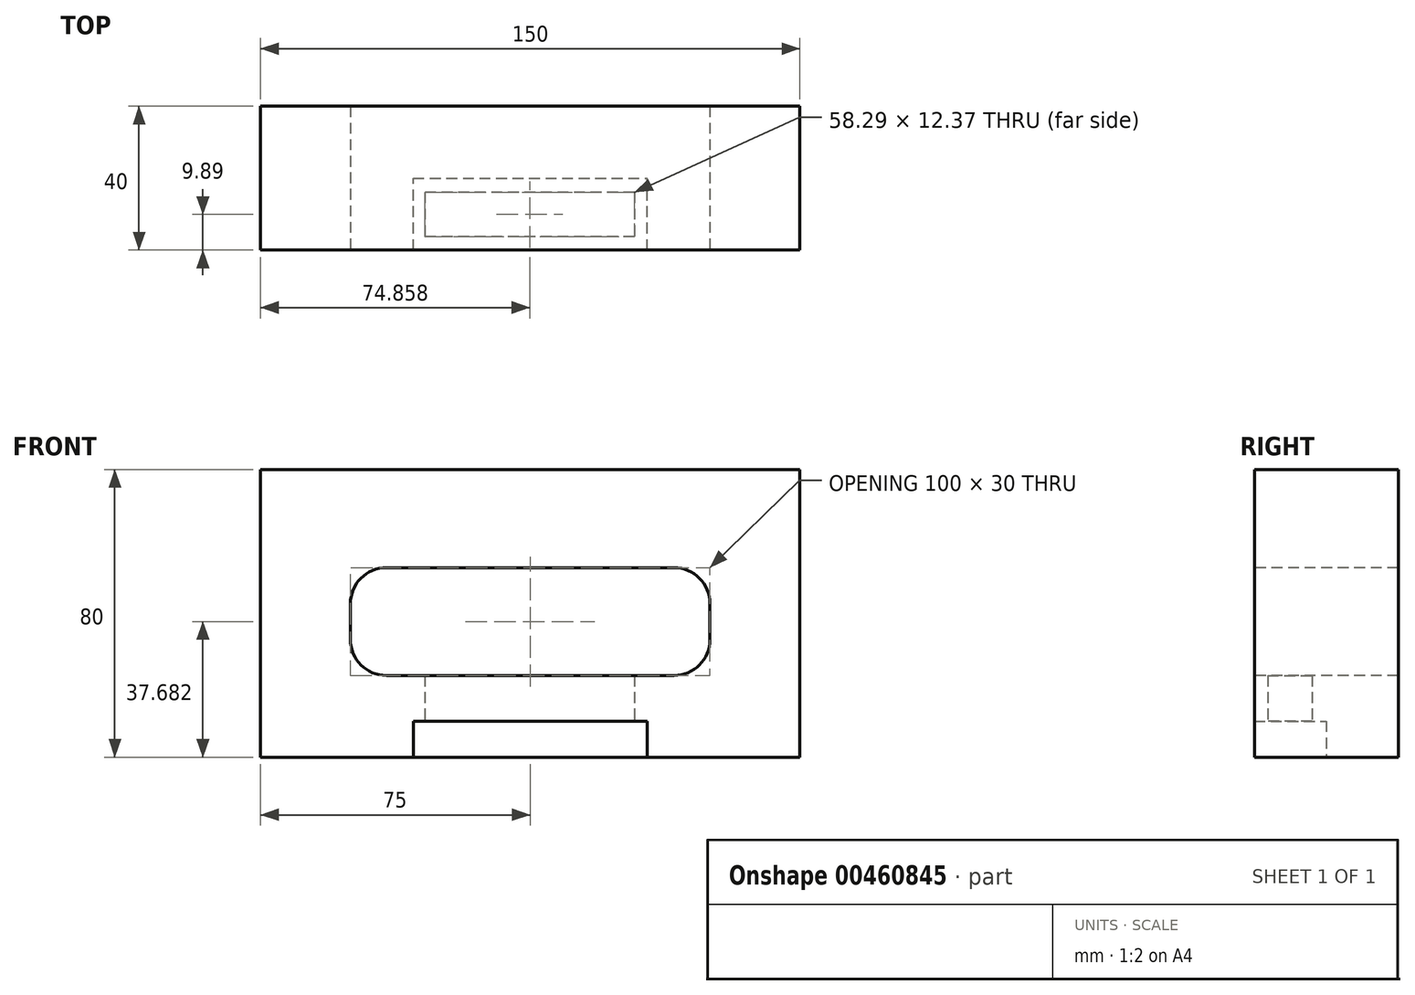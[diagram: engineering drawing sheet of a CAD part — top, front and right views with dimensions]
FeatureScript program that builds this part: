
annotation { "Feature Type Name" : "Feature", "Feature Type Description" : "" }
export const myFeature = defineFeature(function(context is Context, id is Id, definition is map)
    precondition{}
    {
        {
            var Q0;
            Q0=qCreatedBy(makeId("Top.planeOp"),FACE);
            var sketch = newSketch(context, id + "F0", { "sketchPlane" : qUnion([Q0])});
            skLineSegment(sketch, "E0.bottom", {"start": v(75, -20) * mm, "end": v(-75, -20) * mm});
            skLineSegment(sketch, "E0.top", {"start": v(75, 20) * mm, "end": v(-75, 20) * mm});
            skLineSegment(sketch, "E0.left", {"start": v(75, -20) * mm, "end": v(75, 20) * mm});
            skLineSegment(sketch, "E0.right", {"start": v(-75, -20) * mm, "end": v(-75, 20) * mm});
            skPoint(sketch, "E0.middle", {"position": v(0, 0) * mm});
            skSolve(sketch);
        }
        {
            var Q0;
            Q0=makeQuery(id+"F0.imprint","IMPRINT",FACE,{"disambiguationData":[TD([[makeQuery(id+"F0.imprint","IMPRINT",EDGE,{"derivedFrom":sQuery(id+"F0.wireOp",EDGE,"E0.bottom")}),-1.0]])]});
            extrude(context, id + "F1", {"entities" : qUnion([Q0]), "depth" : 80 * mm});
        }
        {
            var Q0;
            Q0=makeQuery(id+"F1.opExtrude","CAP_FACE",FACE,{"disambiguationData":[OSD([sQuery(id+"F0.wireOp",EDGE,"E0.bottom"),sQuery(id+"F0.wireOp",EDGE,"E0.top"),sQuery(id+"F0.wireOp",EDGE,"E0.left"),sQuery(id+"F0.wireOp",EDGE,"E0.right")])],"isStart":true});
            var sketch = newSketch(context, id + "F2", { "sketchPlane" : qUnion([Q0])});
            skLineSegment(sketch, "E1.bottom", {"start": v(-32.5, 20) * mm, "end": v(32.5, 20) * mm});
            skLineSegment(sketch, "E1.top", {"start": v(-32.5, 0) * mm, "end": v(32.5, 0) * mm});
            skLineSegment(sketch, "E1.left", {"start": v(-32.5, 20) * mm, "end": v(-32.5, 0) * mm});
            skLineSegment(sketch, "E1.right", {"start": v(32.5, 20) * mm, "end": v(32.5, 0) * mm});
            skSolve(sketch);
        }
        {
            var Q0;
            Q0 = qSketchRegion(id + "F2", true);
            extrude(context, id + "F3", {"entities" : qUnion([Q0]), "operationType" : NewBodyOperationType.REMOVE, "oppositeDirection" : true, "depth" : 10 * mm});
        }
        {
            var Q0;
            Q0=makeQuery(id+"F1.opExtrude","SWEPT_FACE",FACE,{"disambiguationData":[OSD([sQuery(id+"F0.wireOp",EDGE,"E0.bottom")])]});
            var sketch = newSketch(context, id + "F4", { "sketchPlane" : qUnion([Q0])});
            skLineSegment(sketch, "E2.bottom", {"start": v(40, 22.68) * mm, "end": v(-40, 22.68) * mm});
            skLineSegment(sketch, "E2.top", {"start": v(40, 52.68) * mm, "end": v(-40, 52.68) * mm});
            skLineSegment(sketch, "E2.left", {"start": v(50, 32.68) * mm, "end": v(50, 42.68) * mm});
            skLineSegment(sketch, "E2.right", {"start": v(-50, 32.68) * mm, "end": v(-50, 42.68) * mm});
            skPoint(sketch, "E3.visualSharp", {"position": v(50, 22.68) * mm});
            skArc(sketch, "E3.filletArc", {"start": v(40, 22.68) * mm, "mid": v(47.07, 25.61) * mm, "end": v(50, 32.68) * mm});
            skPoint(sketch, "E4.visualSharp", {"position": v(50, 52.68) * mm});
            skArc(sketch, "E4.filletArc", {"start": v(50, 42.68) * mm, "mid": v(47.07, 49.75) * mm, "end": v(40, 52.68) * mm});
            skPoint(sketch, "E5.visualSharp", {"position": v(-50, 52.68) * mm});
            skArc(sketch, "E5.filletArc", {"start": v(-40, 52.68) * mm, "mid": v(-47.07, 49.75) * mm, "end": v(-50, 42.68) * mm});
            skPoint(sketch, "E6.visualSharp", {"position": v(-50, 22.68) * mm});
            skArc(sketch, "E6.filletArc", {"start": v(-50, 32.68) * mm, "mid": v(-47.07, 25.61) * mm, "end": v(-40, 22.68) * mm});
            skSolve(sketch);
        }
        {
            var Q0;
            Q0 = qSketchRegion(id + "F4", true);
            extrude(context, id + "F5", {"entities" : qUnion([Q0]), "operationType" : NewBodyOperationType.REMOVE, "oppositeDirection" : true, "depth" : 264.4 * mm});
        }
        {
            var Q0;
            Q0=makeQuery(id+"F3.boolean.opBoolean","COPY",FACE,{"derivedFrom":makeQuery(id+"F3.opExtrude","CAP_FACE",FACE,{"disambiguationData":[OSD([sQuery(id+"F2.wireOp",EDGE,"E1.bottom"),sQuery(id+"F2.wireOp",EDGE,"E1.top"),sQuery(id+"F2.wireOp",EDGE,"E1.left"),sQuery(id+"F2.wireOp",EDGE,"E1.right")])],"isStart":false})});
            var sketch = newSketch(context, id + "F6", { "sketchPlane" : qUnion([Q0])});
            skLineSegment(sketch, "E7.bottom", {"start": v(29, 3.92) * mm, "end": v(-29.29, 3.92) * mm});
            skLineSegment(sketch, "E7.top", {"start": v(29, 16.3) * mm, "end": v(-29.29, 16.3) * mm});
            skLineSegment(sketch, "E7.left", {"start": v(29, 3.92) * mm, "end": v(29, 16.3) * mm});
            skLineSegment(sketch, "E7.right", {"start": v(-29.29, 3.92) * mm, "end": v(-29.29, 16.3) * mm});
            skSolve(sketch);
        }
        {
            var Q0;
            Q0 = qSketchRegion(id + "F6", true);
            extrude(context, id + "F7", {"entities" : qUnion([Q0]), "operationType" : NewBodyOperationType.REMOVE, "oppositeDirection" : true, "depth" : 25 * mm});
        }
    });
